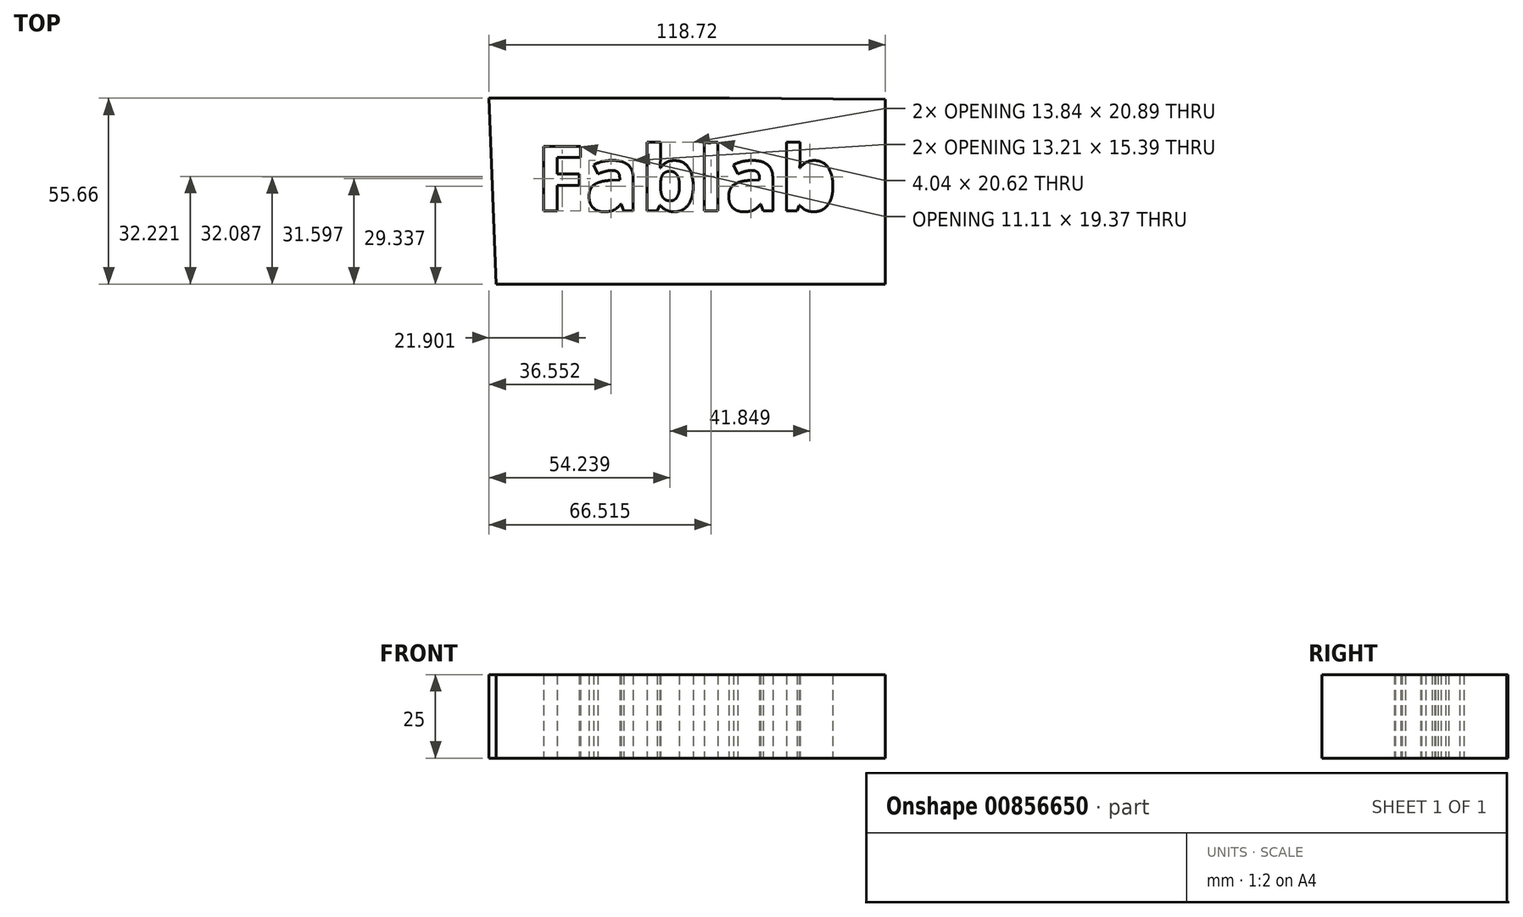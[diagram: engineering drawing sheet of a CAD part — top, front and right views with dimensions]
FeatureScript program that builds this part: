
annotation { "Feature Type Name" : "Feature", "Feature Type Description" : "" }
export const myFeature = defineFeature(function(context is Context, id is Id, definition is map)
    precondition{}
    {
        {
            var Q0;
            Q0=qCreatedBy(makeId("Top.planeOp"),FACE);
            var sketch = newSketch(context, id + "F0", { "sketchPlane" : qUnion([Q0])});
            skLineSegment(sketch, "E0", {"start": v(-29.16, 38.34) * mm, "end": v(42.78, 38.34) * mm});
            skLineSegment(sketch, "E1", {"start": v(42.78, -17.32) * mm, "end": v(-27.09, -17.32) * mm});
            skLineSegment(sketch, "E2", {"start": v(-27.09, -17.32) * mm, "end": v(-29.16, 38.34) * mm});
            skText(sketch, "E3", { "text": "Fablab", "fontName": "OpenSans-Bold.ttf"});
            skLineSegment(sketch, "E4", {"start": v(42.78, -17.32) * mm, "end": v(89.56, -17.32) * mm});
            skLineSegment(sketch, "E5", {"start": v(89.56, -17.32) * mm, "end": v(89.56, 38.04) * mm});
            skLineSegment(sketch, "E6", {"start": v(89.56, 38.04) * mm, "end": v(42.78, 38.34) * mm});
            skLineSegment(sketch, "E7", {"start": v(43.67, 34.79) * mm, "end": v(43.08, 31.53) * mm});
            const initialGuessF0  = {"E3": [-0.01525, 0.00459, 1, 0, 0.01954]};
            skSetInitialGuess(sketch, initialGuessF0);
            skSolve(sketch);
        }
        {
            var Q0;
            Q0=makeQuery(id+"F0.imprint","IMPRINT",FACE,{"disambiguationData":[TD([[makeQuery(id+"F0.imprint","IMPRINT",EDGE,{"derivedFrom":sQuery(id+"F0.wireOp",EDGE,"E0")}),-1.0]])]});
            var Q1;
            Q1=makeQuery(id+"F0.imprint","IMPRINT",FACE,{"disambiguationData":[TD([[makeQuery(id+"F0.imprint","IMPRINT",EDGE,{"derivedFrom":sQuery(id+"F0.wireOp",EDGE,"E3.sketch_text.stroke-49")}),1.0]])]});
            extrude(context, id + "F1", {"entities" : qUnion([Q0, Q1]), "depth" : 25 * mm, "offsetDistance" : 25 * mm});
        }
    });
